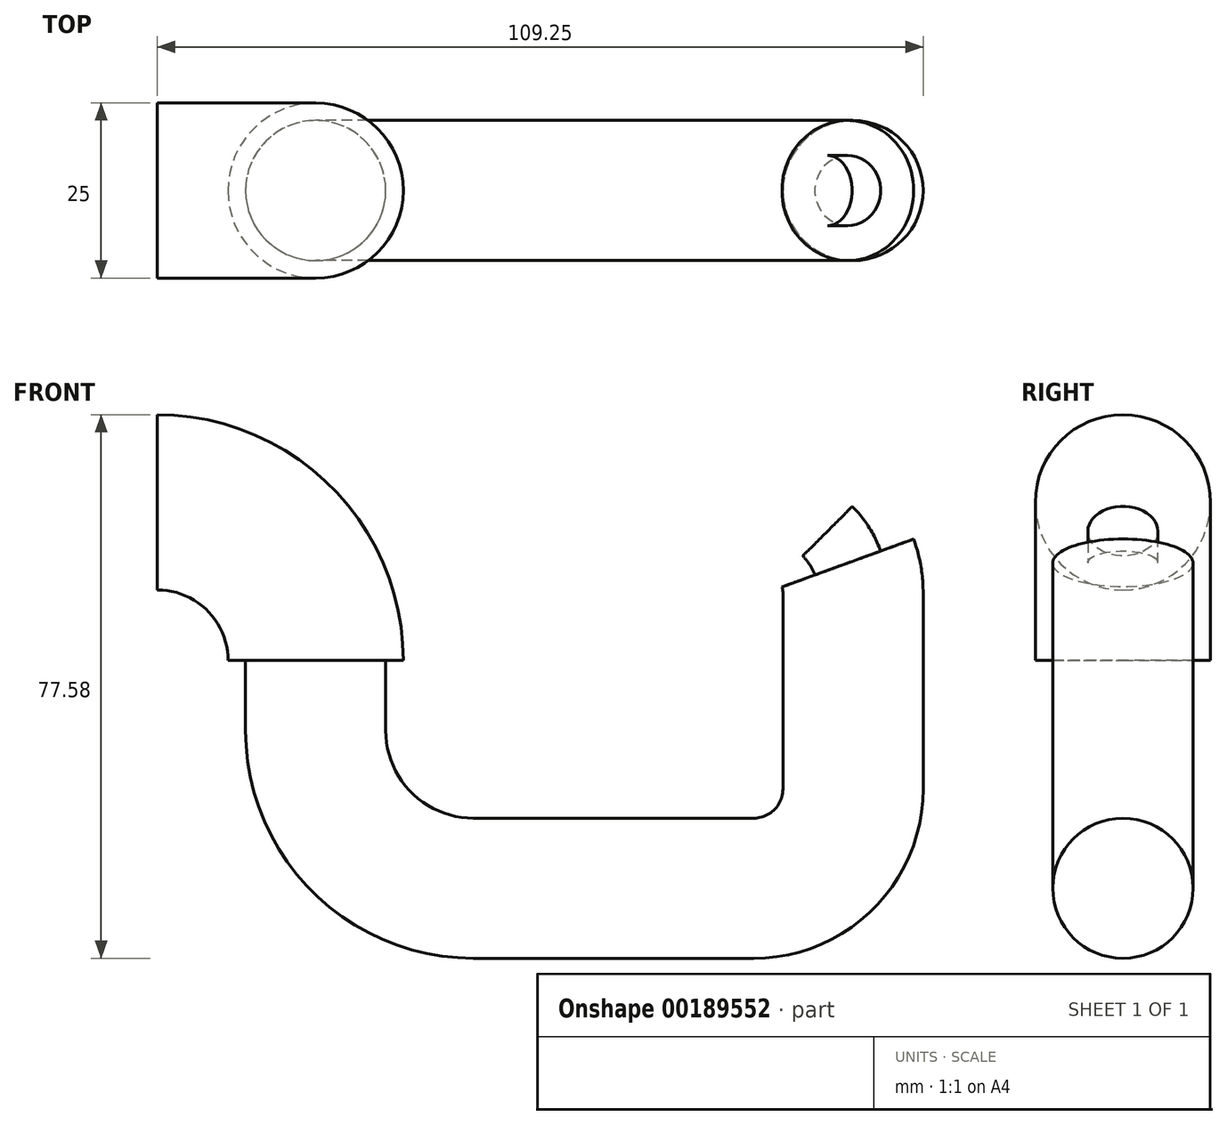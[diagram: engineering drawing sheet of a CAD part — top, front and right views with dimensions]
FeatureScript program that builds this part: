
annotation { "Feature Type Name" : "Feature", "Feature Type Description" : "" }
export const myFeature = defineFeature(function(context is Context, id is Id, definition is map)
    precondition{}
    {
        {
            var Q0;
            Q0=qCreatedBy(makeId("Right.planeOp"),FACE);
            var sketch = newSketch(context, id + "F0", { "sketchPlane" : qUnion([Q0])});
            skCircle(sketch, "E0", {"center": v(0, 0) * mm, "radius": 12.5 * mm});
            skLineSegment(sketch, "E1", {"start": v(0, 0) * mm, "end": v(100, 0) * mm});
            skSolve(sketch);
        }
        {
            var Q0;
            Q0=qCreatedBy(makeId("Right.planeOp"),FACE);
            var sketch = newSketch(context, id + "F1", { "sketchPlane" : qUnion([Q0])});
            skLineSegment(sketch, "E2", {"start": v(0, 0) * mm, "end": v(0, -22.59) * mm});
            skLineSegment(sketch, "E3", {"start": v(-33.96, -22.59) * mm, "end": v(50.14, -22.59) * mm});
            skSolve(sketch);
        }
        {
            var Q0;
            Q0=makeQuery(id+"F0.imprint","IMPRINT",FACE,{"disambiguationData":[TD([[makeQuery(id+"F0.imprint","IMPRINT",EDGE,{"derivedFrom":sQuery(id+"F0.wireOp",EDGE,"E0")}),1.0]])]});
            var Q1;
            Q1=sQuery(id+"F1.wireOp",EDGE,"E3");
            revolve(context, id + "F2", {"entities" : qUnion([Q0]), "axis" : qUnion([Q1]), "revolveType" : RevolveType.ONE_DIRECTION, "angle" : 90 * degree});
        }
        {
            var Q0;
            Q0=makeQuery(id+"F2.opRevolve","CAP_FACE",FACE,{"disambiguationData":[OSD([sQuery(id+"F0.wireOp",EDGE,"E0")])],"isStart":false});
            var sketch = newSketch(context, id + "F3", { "sketchPlane" : qUnion([Q0])});
            skCircle(sketch, "E4", {"center": v(22.59, 0) * mm, "radius": 10 * mm});
            skSolve(sketch);
        }
        {
            var Q0;
            Q0=makeQuery(id+"F3.imprint","IMPRINT",FACE,{"disambiguationData":[TD([[makeQuery(id+"F3.imprint","IMPRINT",EDGE,{"derivedFrom":sQuery(id+"F3.wireOp",EDGE,"E4")}),1.0]])]});
            extrude(context, id + "F4", {"entities" : qUnion([Q0]), "operationType" : NewBodyOperationType.ADD, "depth" : 10 * mm});
        }
        {
            var Q0;
            Q0=makeQuery(id+"F4.opExtrude","CAP_FACE",FACE,{"disambiguationData":[OSD([sQuery(id+"F3.wireOp",EDGE,"E4")])],"isStart":false});
            var sketch = newSketch(context, id + "F5", { "sketchPlane" : qUnion([Q0])});
            skSolve(sketch);
        }
        {
            var Q0;
            Q0=makeQuery(id+"F2.opRevolve","CAP_FACE",FACE,{"disambiguationData":[OSD([sQuery(id+"F0.wireOp",EDGE,"E0")])],"isStart":false});
            var Q1;
            Q1=makeQuery(id+"F4.opExtrude","CAP_FACE",FACE,{"disambiguationData":[OSD([sQuery(id+"F3.wireOp",EDGE,"E4")])],"isStart":false});
            var Q2;
            Q2=makeQuery(id+"F2.opRevolve","CAP_EDGE",EDGE,{"disambiguationData":[OSD([sQuery(id+"F0.wireOp",EDGE,"E0")])],"isStart":false});
            var Q3;
            Q3=makeQuery(id+"F4.opExtrude","CAP_EDGE",EDGE,{"disambiguationData":[OSD([sQuery(id+"F3.wireOp",EDGE,"E4")])],"isStart":false});
            loft(context, id + "F6", {"bodyType" : ToolBodyType.SURFACE, "operationType" : NewBodyOperationType.REMOVE, "sheetProfilesArray" : [{ "sheetProfileEntities" : qUnion([Q0]) }, { "sheetProfileEntities" : qUnion([Q1]) }], "wireProfilesArray" : [{ "wireProfileEntities" : qUnion([Q2]) }, { "wireProfileEntities" : qUnion([Q3]) }]});
        }
        {
            var Q0;
            Q0=makeQuery(id+"F5.imprint","IMPRINT",FACE,{"disambiguationData":[TD([[makeQuery(id+"F5.imprint","IMPRINT",EDGE,{"derivedFrom":makeQuery(id+"F4.opExtrude","CAP_EDGE",EDGE,{"disambiguationData":[OSD([sQuery(id+"F3.wireOp",EDGE,"E4")])],"isStart":false})}),1.0]])]});
            var sketch = newSketch(context, id + "F7", { "sketchPlane" : qUnion([Q0])});
            skLineSegment(sketch, "E5", {"start": v(38.46, 0) * mm, "end": v(45.08, 0) * mm});
            skLineSegment(sketch, "E6", {"start": v(45.08, 45.8) * mm, "end": v(45.08, -50.06) * mm});
            skSolve(sketch);
        }
        {
            var Q0;
            Q0=makeQuery(id+"F5.imprint","IMPRINT",FACE,{"disambiguationData":[TD([[makeQuery(id+"F5.imprint","IMPRINT",EDGE,{"derivedFrom":makeQuery(id+"F4.opExtrude","CAP_EDGE",EDGE,{"disambiguationData":[OSD([sQuery(id+"F3.wireOp",EDGE,"E4")])],"isStart":false})}),1.0]])]});
            var Q1;
            Q1=sQuery(id+"F7.wireOp",EDGE,"E6");
            revolve(context, id + "F8", {"operationType" : NewBodyOperationType.ADD, "entities" : qUnion([Q0]), "axis" : qUnion([Q1]), "revolveType" : RevolveType.ONE_DIRECTION, "oppositeDirection" : true, "angle" : 90 * degree});
        }
        {
            var Q0;
            Q0=makeQuery(id+"F8.opRevolve","CAP_FACE",FACE,{"disambiguationData":[OSD([sQuery(id+"F3.wireOp",EDGE,"E4")])],"isStart":false});
            var sketch = newSketch(context, id + "F9", { "sketchPlane" : qUnion([Q0])});
            skSolve(sketch);
        }
        {
            var Q0;
            Q0=makeQuery(id+"F9.imprint","IMPRINT",FACE,{"disambiguationData":[TD([[makeQuery(id+"F9.imprint","IMPRINT",EDGE,{"derivedFrom":makeQuery(id+"F8.opRevolve","CAP_EDGE",EDGE,{"disambiguationData":[OSD([sQuery(id+"F3.wireOp",EDGE,"E4")])],"isStart":false})}),1.0]])]});
            extrude(context, id + "F10", {"entities" : qUnion([Q0]), "operationType" : NewBodyOperationType.ADD, "depth" : 40 * mm});
        }
        {
            var Q0;
            Q0=makeQuery(id+"F10.opExtrude","CAP_FACE",FACE,{"disambiguationData":[OSD([sQuery(id+"F3.wireOp",EDGE,"E4")])],"isStart":false});
            var sketch = newSketch(context, id + "F11", { "sketchPlane" : qUnion([Q0])});
            skLineSegment(sketch, "E7", {"start": v(0, -55.08) * mm, "end": v(0, -40.92) * mm});
            skLineSegment(sketch, "E8", {"start": v(-22.18, -40.92) * mm, "end": v(24.82, -40.92) * mm});
            skSolve(sketch);
        }
        {
            var Q0;
            Q0=makeQuery(id+"F11.imprint","IMPRINT",FACE,{"disambiguationData":[TD([[makeQuery(id+"F11.imprint","IMPRINT",EDGE,{"derivedFrom":makeQuery(id+"F10.opExtrude","CAP_EDGE",EDGE,{"disambiguationData":[OSD([sQuery(id+"F3.wireOp",EDGE,"E4")])],"isStart":false})}),1.0]])]});
            var Q1;
            Q1=sQuery(id+"F11.wireOp",EDGE,"E8");
            revolve(context, id + "F12", {"operationType" : NewBodyOperationType.ADD, "entities" : qUnion([Q0]), "axis" : qUnion([Q1]), "revolveType" : RevolveType.ONE_DIRECTION, "oppositeDirection" : true, "angle" : 90 * degree});
        }
        {
            var Q0;
            Q0=makeQuery(id+"F12.opRevolve","CAP_FACE",FACE,{"disambiguationData":[OSD([sQuery(id+"F3.wireOp",EDGE,"E4")])],"isStart":false});
            var sketch = newSketch(context, id + "F13", { "sketchPlane" : qUnion([Q0])});
            skSolve(sketch);
        }
        {
            var Q0;
            Q0=makeQuery(id+"F13.imprint","IMPRINT",FACE,{"disambiguationData":[TD([[makeQuery(id+"F13.imprint","IMPRINT",EDGE,{"derivedFrom":makeQuery(id+"F12.opRevolve","CAP_EDGE",EDGE,{"disambiguationData":[OSD([sQuery(id+"F3.wireOp",EDGE,"E4")])],"isStart":false})}),1.0]])]});
            extrude(context, id + "F14", {"entities" : qUnion([Q0]), "operationType" : NewBodyOperationType.ADD, "depth" : 28 * mm});
        }
        {
            var Q0;
            Q0=makeQuery(id+"F14.opExtrude","CAP_FACE",FACE,{"disambiguationData":[OSD([sQuery(id+"F3.wireOp",EDGE,"E4")])],"isStart":false});
            var sketch = newSketch(context, id + "F15", { "sketchPlane" : qUnion([Q0])});
            skCircle(sketch, "E9", {"center": v(99.25, 0) * mm, "radius": 5 * mm});
            skSolve(sketch);
        }
        {
            var Q0;
            Q0=makeQuery(id+"F15.imprint","IMPRINT",FACE,{"disambiguationData":[TD([[makeQuery(id+"F15.imprint","IMPRINT",EDGE,{"derivedFrom":sQuery(id+"F15.wireOp",EDGE,"E9")}),1.0]])]});
            var sketch = newSketch(context, id + "F16", { "sketchPlane" : qUnion([Q0])});
            skLineSegment(sketch, "E10", {"start": v(99.55, 0) * mm, "end": v(86.8, 0) * mm});
            skLineSegment(sketch, "E11", {"start": v(86.8, 22.21) * mm, "end": v(86.8, -24.6) * mm});
            skSolve(sketch);
        }
        {
            var Q0;
            Q0=makeQuery(id+"F15.imprint","IMPRINT",FACE,{"disambiguationData":[TD([[makeQuery(id+"F15.imprint","IMPRINT",EDGE,{"derivedFrom":sQuery(id+"F15.wireOp",EDGE,"E9")}),-1.0]])]});
            var Q1;
            Q1=sQuery(id+"F16.wireOp",EDGE,"E11");
            revolve(context, id + "F17", {"operationType" : NewBodyOperationType.ADD, "entities" : qUnion([Q0]), "axis" : qUnion([Q1]), "revolveType" : RevolveType.ONE_DIRECTION, "angle" : 20 * degree});
        }
        {
            var Q0;
            Q0=makeQuery(id+"F16.imprint","IMPRINT",FACE,{"disambiguationData":[TD([[makeQuery(id+"F16.imprint","IMPRINT",EDGE,{"derivedFrom":makeQuery(id+"F15.imprint","IMPRINT",EDGE,{"derivedFrom":sQuery(id+"F15.wireOp",EDGE,"E9")})}),1.0]])]});
            var Q1;
            Q1=sQuery(id+"F16.wireOp",EDGE,"E11");
            revolve(context, id + "F18", {"operationType" : NewBodyOperationType.ADD, "entities" : qUnion([Q0]), "axis" : qUnion([Q1]), "revolveType" : RevolveType.ONE_DIRECTION, "angle" : 45 * degree});
        }
        {
            var Q0;
            Q0=makeQuery(id+"F18.opRevolve","CAP_EDGE",EDGE,{"disambiguationData":[OSD([sQuery(id+"F15.wireOp",EDGE,"E9")])],"isStart":false});
            var Q1;
            Q1=makeQuery(id+"F17.opRevolve","CAP_EDGE",EDGE,{"disambiguationData":[OSD([sQuery(id+"F3.wireOp",EDGE,"E4")])],"isStart":false});
            loft(context, id + "F19", {"bodyType" : ToolBodyType.SURFACE, "wireProfilesArray" : [{ "wireProfileEntities" : qUnion([Q0]) }, { "wireProfileEntities" : qUnion([Q1]) }]});
        }
    });
